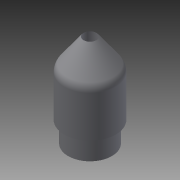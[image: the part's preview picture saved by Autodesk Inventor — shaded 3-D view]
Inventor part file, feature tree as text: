
AUTODESK INVENTOR PART (.ipt)
format: ipt  version: 2014 SP1 (Build 180222100, 222)  size: 103,424 bytes
history: native  units: in
note: dims shown in document units (in); Inventor stores cm internally (conversion verified against a paired STEP export)
features: sketch x2, revolve x1, extrude x1
ambient origin geometry x8: Origin, YZ Plane, XZ Plane, XY Plane, X Axis, Y Axis, Z Axis, Center Point
bodies: Solid1 (feature_tree)
feature tree (4):
  revolve  "Revolution1"  [1 undecoded]
  extrude  "Extrusion1"  TaperAngle=90.0deg  [1 undecoded]
  sketch  "Sketch1"  dims[d0=0.25in d3=0.0625in]
  sketch  "Sketch2"  dims[d4=0.125in d5=90.0deg d6=0.425in d7=0.2in d8=0.0in d9=0.4in d10=0.7in]
note: 2 required parameter values undecoded (feature->parameter linkage not recoverable at this tier; creation-order binding heuristic only, values carry confidence <= 0.55)